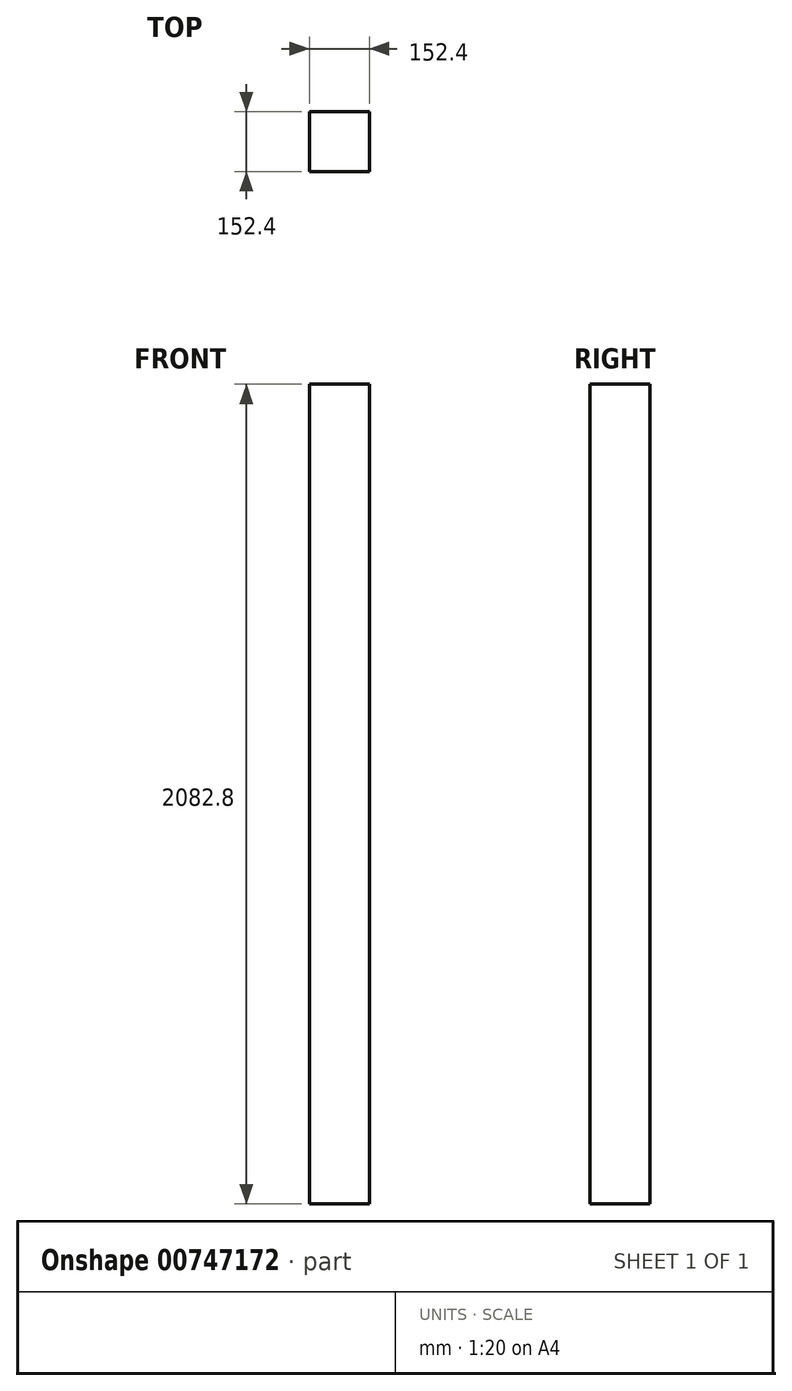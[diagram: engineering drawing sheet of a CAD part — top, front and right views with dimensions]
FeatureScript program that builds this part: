
annotation { "Feature Type Name" : "Feature", "Feature Type Description" : "" }
export const myFeature = defineFeature(function(context is Context, id is Id, definition is map)
    precondition{}
    {
        {
            var Q0;
            Q0=qCreatedBy(makeId("Top.planeOp"),FACE);
            var sketch = newSketch(context, id + "F0", { "sketchPlane" : qUnion([Q0])});
            skLineSegment(sketch, "E0.bottom", {"start": v(-132.6, 19.17) * mm, "end": v(19.8, 19.17) * mm});
            skLineSegment(sketch, "E0.top", {"start": v(-132.6, -133.23) * mm, "end": v(19.8, -133.23) * mm});
            skLineSegment(sketch, "E0.left", {"start": v(-132.6, 19.17) * mm, "end": v(-132.6, -133.23) * mm});
            skLineSegment(sketch, "E0.right", {"start": v(19.8, 19.17) * mm, "end": v(19.8, -133.23) * mm});
            skSolve(sketch);
        }
        {
            var Q0;
            Q0 = qSketchRegion(id + "F0", true);
            extrude(context, id + "F1", {"entities" : qUnion([Q0]), "depth" : 2082.8 * mm, "offsetDistance" : 25.4 * mm});
        }
    });
